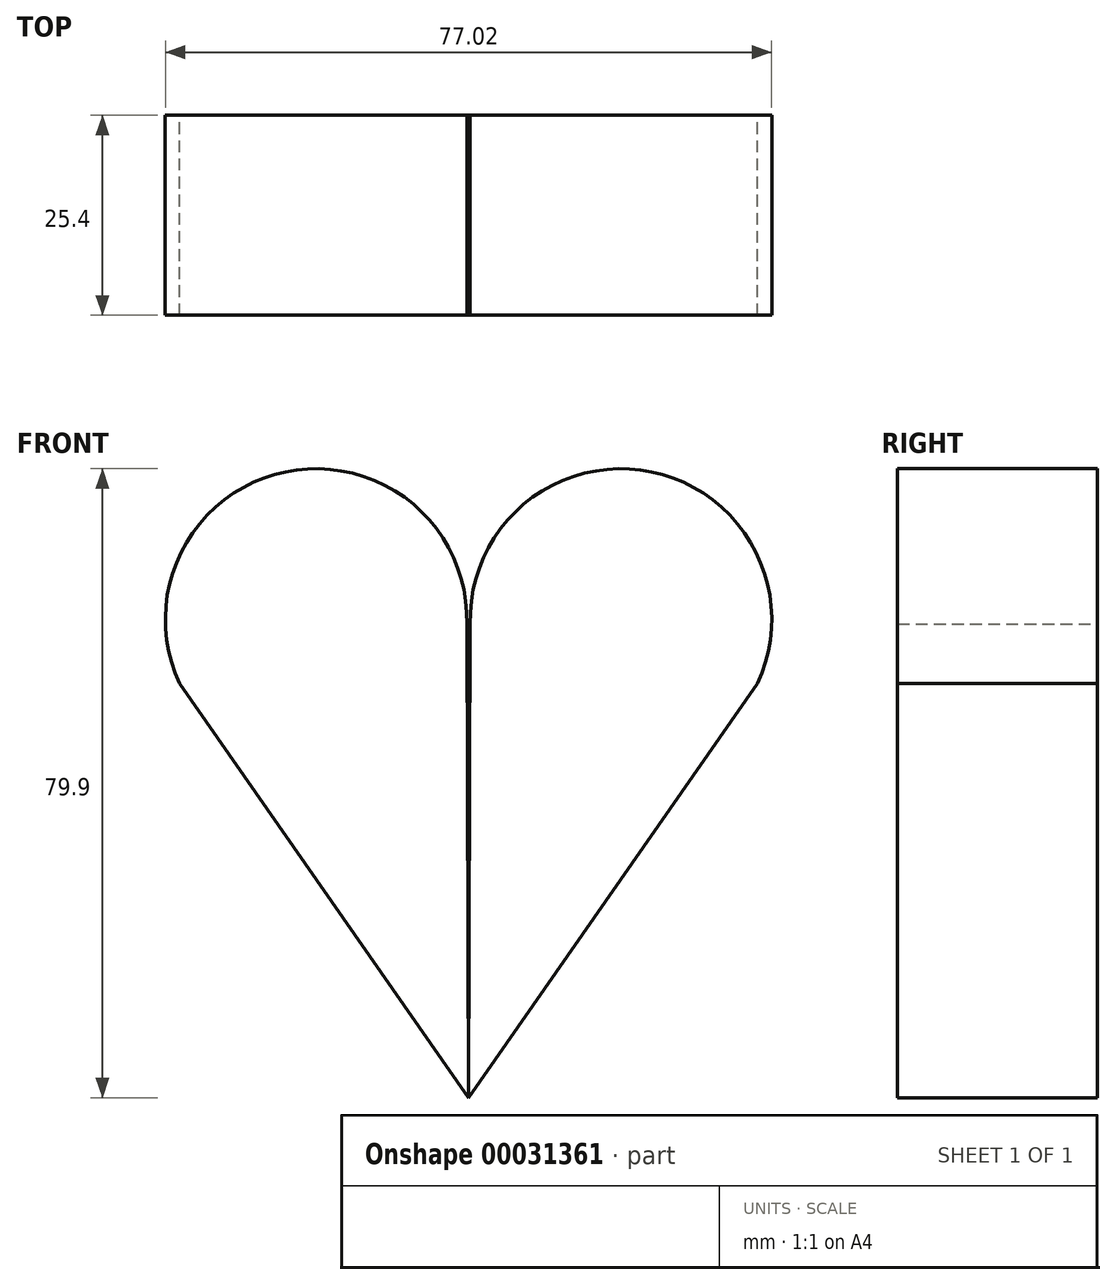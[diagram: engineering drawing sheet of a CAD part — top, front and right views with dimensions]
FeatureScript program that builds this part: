
annotation { "Feature Type Name" : "Feature", "Feature Type Description" : "" }
export const myFeature = defineFeature(function(context is Context, id is Id, definition is map)
    precondition{}
    {
        {
            var Q0;
            Q0=qCreatedBy(makeId("Front.planeOp"),FACE);
            var sketch = newSketch(context, id + "F0", { "sketchPlane" : qUnion([Q0])});
            skCircle(sketch, "E0", {"center": v(19.36, 19.08) * mm, "radius": 19.15 * mm});
            skLineSegment(sketch, "E1", {"start": v(0.22, 18.52) * mm, "end": v(0, -41.67) * mm});
            skLineSegment(sketch, "E2", {"start": v(0, -41.67) * mm, "end": v(36.7, 10.94) * mm});
            skSolve(sketch);
        }
        {
            var Q0;
            {var subQ3=sQuery(id+"F0.wireOp",EDGE,"E1");Q0=makeQuery(id+"F0.imprint","IMPRINT",FACE,{"disambiguationData":[TD([[makeQuery(id+"F0.imprint","IMPRINT",EDGE,{"derivedFrom":subQ3}),1.0]])]});}
            var Q1;
            {var subQ1=sQuery(id+"F0.wireOp",EDGE,"E0");var subQ4=makeQuery(id+"F0.imprint","INTERSECT",VERTEX,{"derivedFrom":[subQ1,sQuery(id+"F0.wireOp",EDGE,"E1")]});Q1=makeQuery(id+"F0.imprint","IMPRINT",FACE,{"disambiguationData":[TD([[makeQuery(id+"F0.imprint","IMPRINT",EDGE,{"disambiguationData":[TD([[subQ4,-1.0]])],"derivedFrom":subQ1}),1.0]])]});}
            extrude(context, id + "F1", {"entities" : qUnion([Q0, Q1]), "depth" : 25.4 * mm});
        }
        {
            var Q0;
            Q0=makeQuery(id+"F1.opExtrude","SWEPT_BODY",BODY,{"disambiguationData":[OSD([sQuery(id+"F0.wireOp",EDGE,"E0"),sQuery(id+"F0.wireOp",EDGE,"E1"),sQuery(id+"F0.wireOp",EDGE,"E2")])]});
            var Q1;
            Q1=qCreatedBy(makeId("Right.planeOp"),FACE);
            mirror(context, id + "F2", {"entities" : qUnion([Q0]), "mirrorPlane" : qUnion([Q1])});
        }
    });
